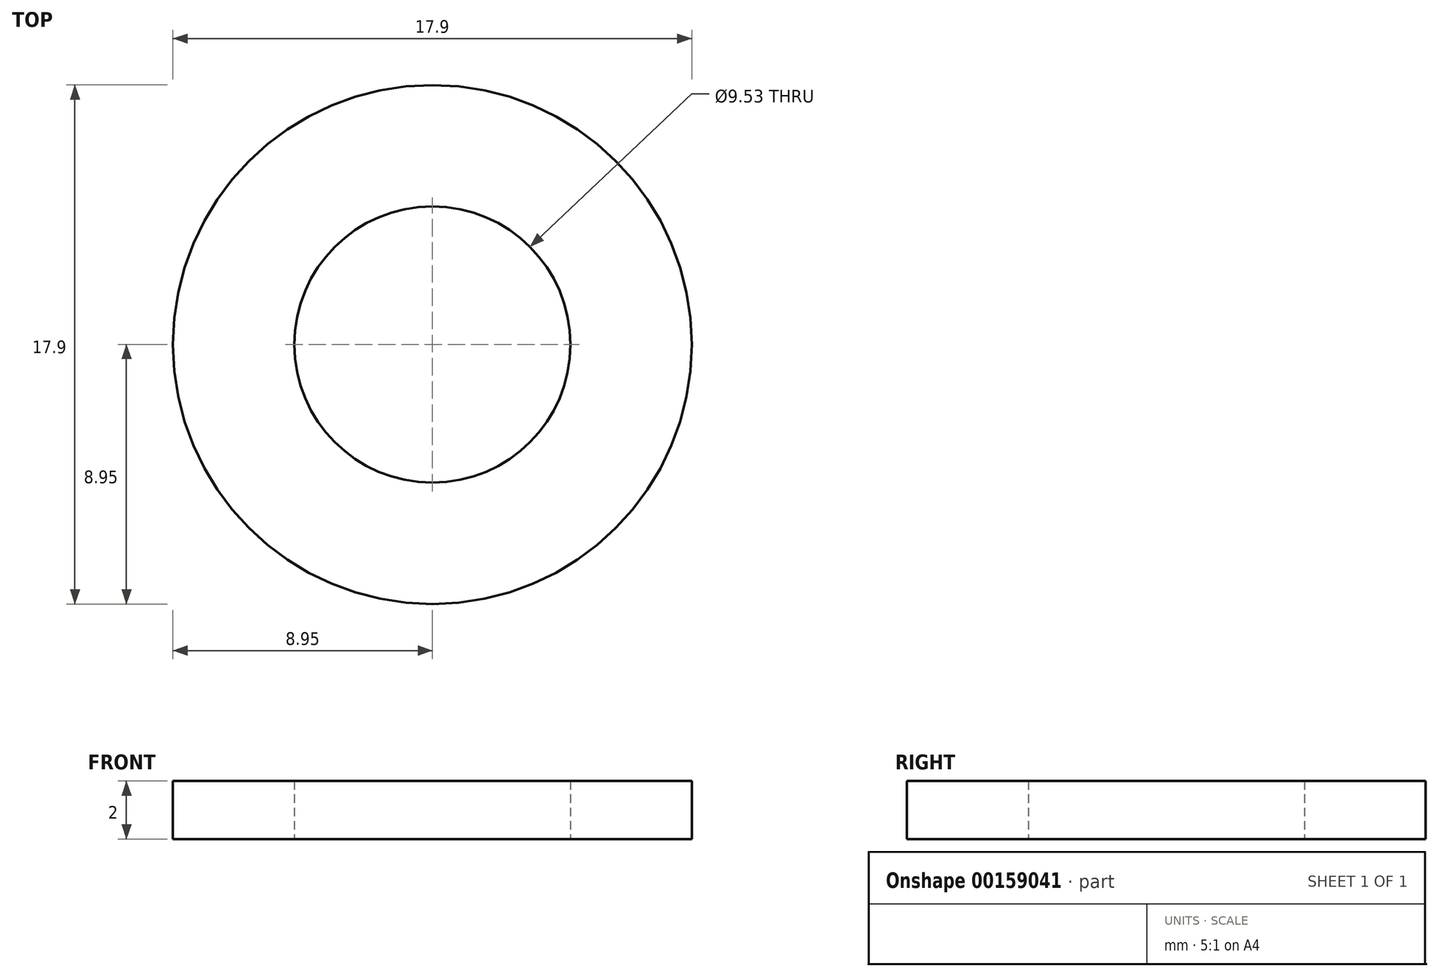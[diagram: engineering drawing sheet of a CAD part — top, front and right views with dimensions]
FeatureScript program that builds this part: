
annotation { "Feature Type Name" : "Feature", "Feature Type Description" : "" }
export const myFeature = defineFeature(function(context is Context, id is Id, definition is map)
    precondition{}
    {
        {
            var Q0;
            Q0=qCreatedBy(makeId("Top.planeOp"),FACE);
            var sketch = newSketch(context, id + "F0", { "sketchPlane" : qUnion([Q0])});
            skCircle(sketch, "E0", {"center": v(0, 0) * mm, "radius": 4.76 * mm});
            skCircle(sketch, "E1", {"center": v(0, 0) * mm, "radius": 8.95 * mm});
            skSolve(sketch);
        }
        {
            var Q0;
            Q0 = qSketchRegion(id + "F0", true);
            extrude(context, id + "F1", {"entities" : qUnion([Q0]), "depth" : 2 * mm});
        }
    });
